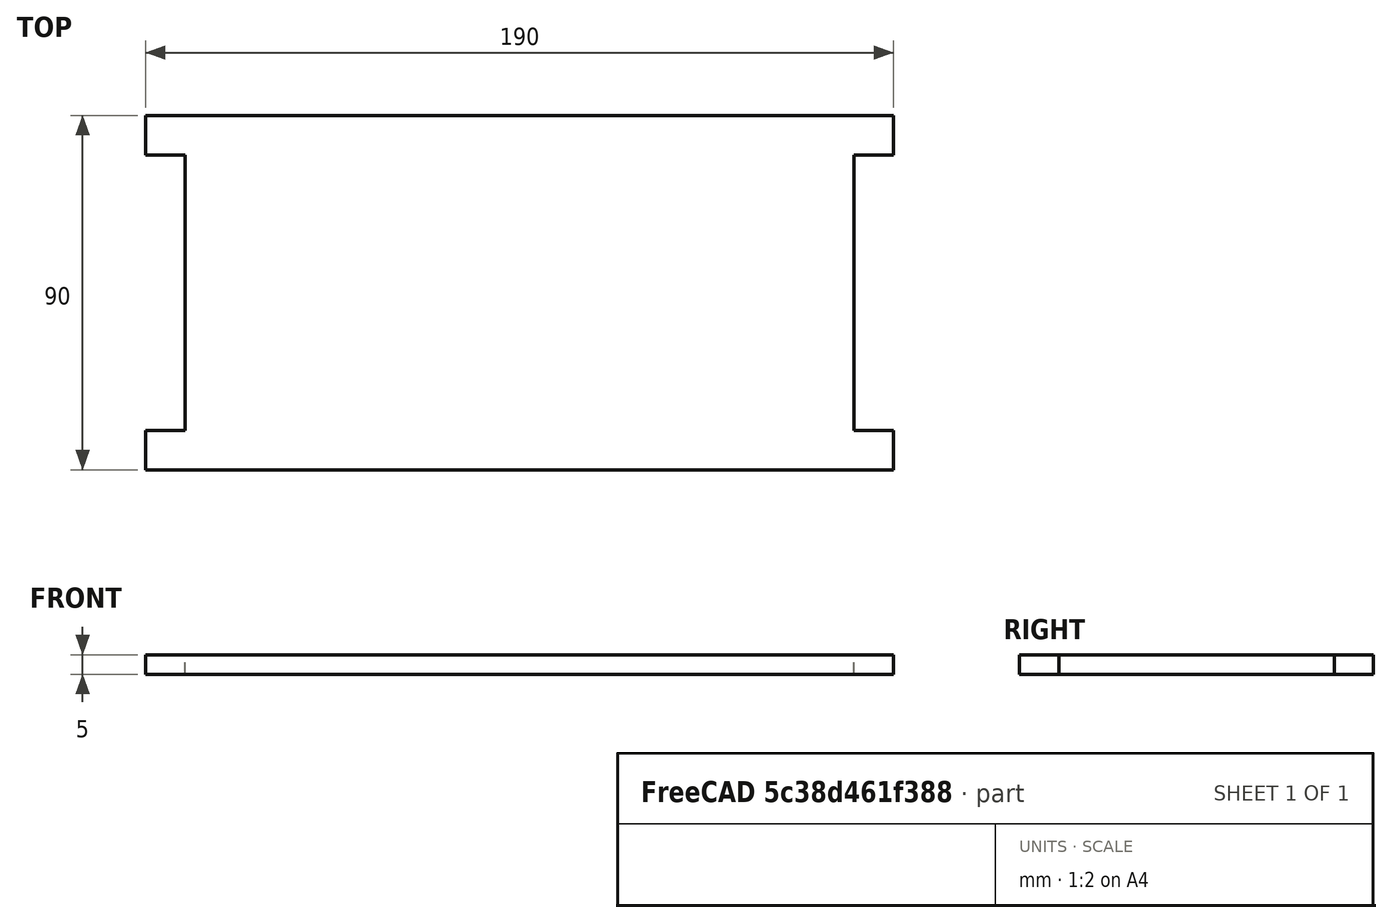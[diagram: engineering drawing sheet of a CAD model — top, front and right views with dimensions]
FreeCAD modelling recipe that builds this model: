
FCSTD DOCUMENT  (FreeCAD 1.0R39109 (Git))
Label: Sled
License: Creative Commons Attribution-ShareAlike 4.0
LicenseURL: https://creativecommons.org/licenses/by-sa/4.0/
objects: Sketcher::SketchObject×3, PartDesign::Pad×1, PartDesign::Body×1
note: 10 computed .brp shape members not serialized (recipe doc carries the construction recipe); baked Part::Feature solids carry a one-line shape summary decoded from their .brp
EXTERNAL_REF file=Variables.FCStd obj=VarSet

FEATURE [Sketcher::SketchObject] Sketch
  ArcFitTolerance = 1e-06
  AttachmentSupport = -> [XY_Plane]
  FullyConstrained = true
  MakeInternals = false
  MapMode = 5
  expr: Constraints[30] = Variables#VarSet.SledLength
  expr: Constraints[31] = Variables#VarSet.SledWidth
  sketch-geometry (12):
    g0: LineSegment StartX=-95 StartY=45 StartZ=0 EndX=95 EndY=45 EndZ=0
    g1: LineSegment StartX=95 StartY=45 StartZ=0 EndX=95 EndY=35 EndZ=0
    g2: LineSegment StartX=95 StartY=35 StartZ=0 EndX=85 EndY=35 EndZ=0
    g3: LineSegment StartX=85 StartY=35 StartZ=0 EndX=85 EndY=-35 EndZ=0
    g4: LineSegment StartX=85 StartY=-35 StartZ=0 EndX=95 EndY=-35 EndZ=0
    g5: LineSegment StartX=95 StartY=-35 StartZ=0 EndX=95 EndY=-45 EndZ=0
    g6: LineSegment StartX=95 StartY=-45 StartZ=0 EndX=-95 EndY=-45 EndZ=0
    g7: LineSegment StartX=-95 StartY=-45 StartZ=0 EndX=-95 EndY=-35 EndZ=0
    g8: LineSegment StartX=-95 StartY=-35 StartZ=0 EndX=-85 EndY=-35 EndZ=0
    g9: LineSegment StartX=-85 StartY=-35 StartZ=0 EndX=-85 EndY=35 EndZ=0
    g10: LineSegment StartX=-85 StartY=35 StartZ=0 EndX=-95 EndY=35 EndZ=0
    g11: LineSegment StartX=-95 StartY=35 StartZ=0 EndX=-95 EndY=45 EndZ=0
  constraints (35):
    c: Horizontal(g0)
    c: Coincident(g0,g1)
    c: Vertical(g1)
    c: Coincident(g1,g2)
    c: Horizontal(g2)
    c: Coincident(g2,g3)
    c: Vertical(g3)
    c: Coincident(g3,g4)
    c: Horizontal(g4)
    c: Coincident(g4,g5)
    c: Vertical(g5)
    c: Coincident(g5,g6)
    c: Horizontal(g6)
    c: Coincident(g6,g7)
    c: Vertical(g7)
    c: Coincident(g7,g8)
    c: Horizontal(g8)
    c: Coincident(g8,g9)
    c: Vertical(g9)
    c: Coincident(g9,g10)
    c: Horizontal(g10)
    c: Coincident(g10,g11)
    c: Coincident(g11,g0)
    c: Vertical(g11)
    c: Vertical(g0,g6)
    c: Vertical(g0,g5)
    c: DistanceY(g10,g0) = 10
    c: Equal(g11,g1)
    c: Equal(g1,g7)
    c: Equal(g7,g5)
    c: DistanceX(g0,g0) = 190
    c: DistanceY(g5,g0) = 90
    c: Symmetric(g0,g5,g-1)
    c: DistanceX(g10,g10) = 10
    c: Equal(g10,g2)
FEATURE [PartDesign::Pad] Pad
  Direction = (0,0,1)
  Length = 5
  Length2 = 10
  Profile = -> Sketch
  ReferenceAxis = -> Sketch [N_Axis]
  Refine = true
  Suppressed = false
  Type = 0
  expr: Length = Variables#VarSet.SledThickness
FEATURE [Sketcher::SketchObject] Sketch001
  ArcFitTolerance = 1e-06
  AttachmentSupport = -> [Pad]
  FullyConstrained = true
  MakeInternals = false
  MapMode = 5
  Placement = pos=(0,0,5) rot=(0,0,1;0rad)
FEATURE [Sketcher::SketchObject] Sketch002
  ArcFitTolerance = 1e-06
  AttachmentSupport = -> [Pad]
  FullyConstrained = true
  MakeInternals = false
  MapMode = 5
  Placement = pos=(0,0,5) rot=(0,0,1;0rad)
FEATURE [PartDesign::Body] Body
  AllowCompound = false
  Group = -> [Sketch,Pad,Sketch001,Sketch002]
  Origin = -> Origin
  Tip = -> Pad
